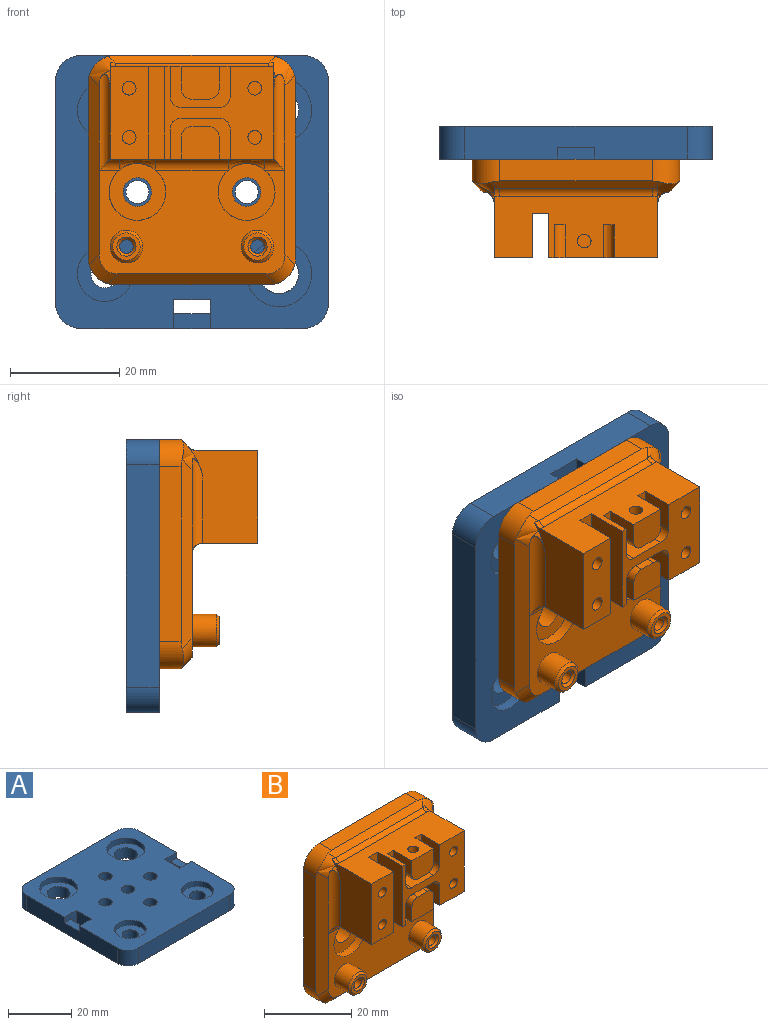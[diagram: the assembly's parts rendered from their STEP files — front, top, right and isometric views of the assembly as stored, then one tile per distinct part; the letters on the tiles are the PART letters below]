
ASSEMBLY  parts=2 mates=1
PART A: 37 faces, bbox 50x50x6 mm
  f0: cylinder r=2.55mm len=5.1mm, axis (0,0,-1), area 64.1mm2, adj f5,f26
  f1: cylinder r=2.55mm len=5.1mm, axis (0,0,-1), area 64.1mm2, adj f5,f24
  f2: cylinder r=3.6mm len=7.2mm, axis (0,0,-1), area 90.5mm2, adj f5,f22
  f3: cylinder r=3.6mm len=7.2mm, axis (0,0,-1), area 90.5mm2, adj f5,f20
  f4: plane 50x50mm, normal (0,0,1), area 1955.5mm2, adj f6,f7,f8,f9,f10,f11,f12,f13
  f5: plane 50x50mm, normal (0,0,-1), area 2256.5mm2, adj f0,f1,f2,f3,f6,f7,f8,f9
  f6: cylinder r=4.63mm len=6mm, axis (0,0,-1), area 43.7mm2, adj f4,f5,f7,f13
  f7: plane 40.73x6mm, normal (-1,0,0), area 229.8mm2, adj f4,f5,f6,f8,f27,f29,f30
  f8: cylinder r=4.63mm len=6mm, axis (0,0,-1), area 43.7mm2, adj f4,f5,f7,f9
  f9: plane 40.73x6mm, normal (0,-1,0), area 244.4mm2, adj f4,f5,f8,f10
  f10: cylinder r=4.63mm len=6mm, axis (0,0,-1), area 43.7mm2, adj f4,f5,f9,f11
  f11: plane 40.73x6mm, normal (1,0,0), area 229.8mm2, adj f4,f5,f10,f12,f31,f32,f34
  f12: cylinder r=4.63mm len=6mm, axis (0,0,-1), area 43.7mm2, adj f4,f5,f11,f13
  f13: plane 40.73x6mm, normal (0,1,0), area 244.4mm2, adj f4,f5,f6,f12
  f14: cylinder r=2.1mm len=6mm, axis (0,0,1), area 79.2mm2, adj f4,f5
  f15: cylinder r=2.1mm len=6mm, axis (0,0,1), area 79.2mm2, adj f4,f5
  f16: cylinder r=2.1mm len=6mm, axis (0,0,1), area 79.2mm2, adj f4,f5
  f17: cylinder r=2.1mm len=6mm, axis (0,0,1), area 79.2mm2, adj f4,f5
  f18: cylinder r=2.1mm len=6mm, axis (0,0,1), area 79.2mm2, adj f4,f5
  f19: cylinder r=6mm len=12mm, axis (0,0,1), area 75.4mm2, adj f4,f20
  f20: plane 12x12mm, normal (0,0,1), area 72.4mm2, adj f3,f19
  f21: cylinder r=6mm len=12mm, axis (0,0,1), area 75.4mm2, adj f4,f22
  f22: plane 12x12mm, normal (0,0,1), area 72.4mm2, adj f2,f21
  f23: cylinder r=5.05mm len=10.1mm, axis (0,0,1), area 63.5mm2, adj f4,f24
  f24: plane 10.1x10.1mm, normal (0,0,1), area 59.7mm2, adj f1,f23
  f25: cylinder r=5.05mm len=10.1mm, axis (0,0,1), area 63.5mm2, adj f4,f26
  f26: plane 10.1x10.1mm, normal (0,0,1), area 59.7mm2, adj f0,f25
  f27: plane 6x5.25mm, normal (0,-1,0), area 21mm2, adj f4,f5,f7,f28,f30,f35
  f28: plane 6.7x6mm, normal (-1,0,0), area 40.2mm2, adj f4,f5,f27,f29
  f29: plane 6x5.25mm, normal (0,1,0), area 21mm2, adj f4,f5,f7,f28,f30,f35
  f30: plane 6.7x2.75mm, normal (0,0,1), area 18.4mm2, adj f7,f27,f29,f35
  f31: plane 6x5.25mm, normal (0,-1,0), area 21mm2, adj f4,f5,f11,f33,f34,f36
  f32: plane 6x5.25mm, normal (0,1,0), area 21mm2, adj f4,f5,f11,f33,f34,f36
  f33: plane 6.7x6mm, normal (1,0,0), area 40.2mm2, adj f4,f5,f31,f32
  f34: plane 6.7x2.75mm, normal (0,0,1), area 18.4mm2, adj f11,f31,f32,f36
  f35: plane 6.7x3.82mm, normal (1,0,0), area 25.6mm2, adj f5,f27,f29,f30
  f36: plane 6.7x3.82mm, normal (-1,0,0), area 25.6mm2, adj f5,f31,f32,f34
PART B: 87 faces, bbox 39.9x19.9x43.9 mm
  f0: plane 35.89x20.89mm, normal (0,-1,0), area 425.8mm2, adj f10,f12,f14,f16,f53,f55,f56,f60
  f1: plane 32x4mm, normal (-1,0,0), area 128mm2, adj f9,f53,f57,f59
  f2: plane 28x4mm, normal (0,0,-1), area 112mm2, adj f9,f55,f59,f63
  f3: plane 32x4mm, normal (1,0,0), area 128mm2, adj f9,f56,f61,f63
  f4: cylinder r=2.6mm len=5.2mm, axis (0,-1,0), area 65.3mm2, adj f9,f13
  f5: cylinder r=1.25mm len=10.5mm, axis (0,-1,0), area 82.5mm2, adj f9,f65
  f6: cylinder r=1.25mm len=10.5mm, axis (0,-1,0), area 82.5mm2, adj f9,f67
  f7: plane 28x4mm, normal (0,0,1), area 112mm2, adj f9,f54,f57,f61
  f8: cylinder r=2.6mm len=5.2mm, axis (0,-1,0), area 65.3mm2, adj f9,f11
  f9: plane 42x38mm, normal (0,1,0), area 1522.2mm2, adj f1,f2,f3,f4,f5,f6,f7,f8
  f10: cylinder r=5.2mm len=10.4mm, axis (0,-1,0), area 65.3mm2, adj f0,f11,f82
  f11: plane 10.4x10.4mm, normal (0,-1,0), area 63.7mm2, adj f8,f10
  f12: cylinder r=5.2mm len=10.4mm, axis (0,-1,0), area 65.3mm2, adj f0,f13,f84
  f13: plane 10.4x10.4mm, normal (0,-1,0), area 63.7mm2, adj f4,f12
  f14: cylinder r=3mm len=6mm, axis (0,1,0), area 84.8mm2, adj f0,f68
  f15: plane 5x5mm, normal (0,-1,0), area 10mm2, adj f67,f68
  f16: cylinder r=3mm len=6mm, axis (0,1,0), area 84.8mm2, adj f0,f66
  f17: plane 5x5mm, normal (0,-1,0), area 10mm2, adj f65,f66
  f18: plane 18.53x13.59mm, normal (-1,0,0), area 174.4mm2, adj f19,f23,f24,f58,f77,f86
  f19: plane 30x10.4mm, normal (0,0,-1), area 249.7mm2, adj f18,f20,f24,f27,f28,f30,f31,f37
  f20: plane 17x8mm, normal (1,0,0), area 136mm2, adj f19,f23,f24,f50
  f21: cylinder r=1.25mm len=12mm, axis (0,1,0), area 94.2mm2, adj f24,f25
  f22: cylinder r=1.25mm len=12mm, axis (0,1,0), area 94.2mm2, adj f24,f26
  f23: plane 30x11.23mm, normal (0,0,1), area 282.3mm2, adj f18,f20,f24,f27,f31,f32,f34,f37
  f24: plane 17x7mm, normal (0,-1,0), area 109.2mm2, adj f18,f19,f20,f21,f22,f23
  f25: plane 2.5x2.5mm, normal (0,-1,0), area 4.9mm2, adj f21
  f26: plane 2.5x2.5mm, normal (0,-1,0), area 4.9mm2, adj f22
  f27: plane 17x8mm, normal (-1,0,0), area 136mm2, adj f19,f23,f37,f50
  f28: plane 6x5.5mm, normal (1,0,0), area 33mm2, adj f19,f37,f49,f74
  f29: plane 7x6mm, normal (0,0,-1), area 42mm2, adj f37,f49,f73,f74
  f30: plane 6x5.5mm, normal (-1,0,0), area 33mm2, adj f19,f37,f49,f73
  f31: plane 18.53x13.59mm, normal (1,0,0), area 174.4mm2, adj f19,f23,f37,f62,f79,f80
  f32: plane 6x5.5mm, normal (-1,0,0), area 33mm2, adj f23,f37,f48,f72
  f33: plane 7x6mm, normal (0,0,1), area 42mm2, adj f37,f48,f71,f72
  f34: plane 6x5.5mm, normal (1,0,0), area 33mm2, adj f23,f37,f48,f71
  f35: cylinder r=1.25mm len=12mm, axis (0,1,0), area 94.2mm2, adj f37,f39
  f36: cylinder r=1.25mm len=12mm, axis (0,1,0), area 94.2mm2, adj f37,f38
  f37: plane 20x17mm, normal (0,-1,0), area 168.6mm2, adj f19,f23,f27,f28,f29,f30,f31,f32
  f38: plane 2.5x2.5mm, normal (0,-1,0), area 4.9mm2, adj f36
  f39: plane 2.5x2.5mm, normal (0,-1,0), area 4.9mm2, adj f35
  f40: plane 6x4mm, normal (-1,0,0), area 24mm2, adj f23,f43,f48,f75
  f41: plane 6x3mm, normal (0,0,-1), area 13.1mm2, adj f43,f48,f51,f75,f76
  f42: plane 6x4mm, normal (1,0,0), area 24mm2, adj f23,f43,f48,f76
  f43: plane 7x6mm, normal (0,-1,0), area 40.3mm2, adj f23,f40,f41,f42,f75,f76
  f44: plane 6x4mm, normal (-1,0,0), area 24mm2, adj f19,f47,f49,f69
  f45: plane 6x4mm, normal (1,0,0), area 24mm2, adj f19,f47,f49,f70
  f46: plane 6x3mm, normal (0,0,1), area 13.1mm2, adj f47,f49,f52,f69,f70
  f47: plane 7x6mm, normal (0,-1,0), area 40.3mm2, adj f19,f44,f45,f46,f69,f70
  f48: plane 11x7.5mm, normal (0,-1,0), area 40.5mm2, adj f23,f32,f33,f34,f40,f41,f42,f71
  f49: plane 11x7.5mm, normal (0,-1,0), area 40.5mm2, adj f19,f28,f29,f30,f44,f45,f46,f69
  f50: plane 17x3mm, normal (0,-1,0), area 51mm2, adj f19,f20,f23,f27
  f51: cylinder r=1.25mm len=6mm, axis (0,0,1), area 47.1mm2, adj f23,f41
  f52: cylinder r=1.25mm len=6mm, axis (0,0,-1), area 47.1mm2, adj f19,f46
  f53: plane 34.67x2.08mm, normal (-0.71,-0.71,0), area 92.9mm2, adj f0,f1,f57,f58,f59,f60,f86
  f54: plane 30.67x1.5mm, normal (0,-0.71,0.71), area 58.8mm2, adj f7,f57,f58,f61,f62,f78
  f55: plane 30.67x2.08mm, normal (0,-0.71,-0.71), area 81.6mm2, adj f0,f2,f59,f60,f63,f64
  f56: plane 34.67x2.08mm, normal (0.71,-0.71,0), area 92.9mm2, adj f0,f3,f61,f62,f63,f64,f80
  f57: cylinder r=5mm len=5mm, axis (0,1,0), area 32.5mm2, adj f1,f7,f9,f53,f54,f58
  f58: cylinder r=5mm len=7.37mm, axis (-0.58,0.58,0.58), area 12.9mm2, adj f18,f53,f54,f57,f77,f86
  f59: cylinder r=5mm len=5mm, axis (0,-1,0), area 32.5mm2, adj f1,f2,f9,f53,f55,f60
  f60: cylinder r=5mm len=5.37mm, axis (-0.58,0.58,-0.58), area 16.6mm2, adj f0,f53,f55,f59
  f61: cylinder r=5mm len=5mm, axis (0,-1,0), area 32.5mm2, adj f3,f7,f9,f54,f56,f62
  f62: cylinder r=5mm len=7.37mm, axis (-0.58,-0.58,-0.58), area 12.9mm2, adj f31,f54,f56,f61,f79,f80
  f63: cylinder r=5mm len=5mm, axis (0,1,0), area 32.5mm2, adj f2,f3,f9,f55,f56,f64
  f64: cylinder r=5mm len=5.37mm, axis (-0.58,-0.58,0.58), area 16.6mm2, adj f0,f55,f56,f63
  f65: cone r=1.25mm half-angle=45deg, axis (0,-1,0), area 6.7mm2, adj f5,f17
  f66: cone r=2.5mm half-angle=45deg, axis (0,1,0), area 12.2mm2, adj f16,f17
  f67: cone r=1.25mm half-angle=45deg, axis (0,-1,0), area 6.7mm2, adj f6,f15
  f68: cone r=2.5mm half-angle=45deg, axis (0,1,0), area 12.2mm2, adj f14,f15
  f69: cylinder r=2mm len=6mm, axis (0,1,0), area 18.8mm2, adj f44,f46,f47,f49
  f70: cylinder r=2mm len=6mm, axis (0,1,0), area 18.8mm2, adj f45,f46,f47,f49
  f71: cylinder r=2mm len=6mm, axis (0,-1,0), area 18.8mm2, adj f33,f34,f37,f48
  f72: cylinder r=2mm len=6mm, axis (0,1,0), area 18.8mm2, adj f32,f33,f37,f48
  f73: cylinder r=2mm len=6mm, axis (0,-1,0), area 18.8mm2, adj f29,f30,f37,f49
  f74: cylinder r=2mm len=6mm, axis (0,-1,0), area 18.8mm2, adj f28,f29,f37,f49
  f75: cylinder r=2mm len=6mm, axis (0,1,0), area 18.8mm2, adj f40,f41,f43,f48
  f76: cylinder r=2mm len=6mm, axis (0,-1,0), area 18.8mm2, adj f41,f42,f43,f48
  f77: bspline ~1.59x1.16mm, area 1.6mm2, adj f18,f23,f58,f78
  f78: cylinder r=2mm len=28.1mm, axis (-1,0,0), area 44.1mm2, adj f23,f54,f77,f79
  f79: bspline ~1.59x1.16mm, area 1.6mm2, adj f23,f31,f62,f78
  f80: cylinder r=2mm len=17.55mm, axis (0,0,1), area 49.4mm2, adj f31,f56,f62,f81
  f81: cylinder r=2mm len=3.68mm, axis (1,0,0), area 8.4mm2, adj f0,f19,f80,f82
  f82: bspline ~6.65x2mm, area 15.3mm2, adj f10,f19,f81,f83
  f83: cylinder r=2mm len=13.35mm, axis (1,0,0), area 42mm2, adj f0,f19,f82,f84
  f84: bspline ~6.65x2mm, area 15.3mm2, adj f12,f19,f83,f85
  f85: cylinder r=2mm len=3.68mm, axis (1,0,0), area 8.4mm2, adj f0,f19,f84,f86
  f86: cylinder r=2mm len=17.55mm, axis (0,0,-1), area 49.4mm2, adj f18,f53,f58,f85
PLACE A rot(axis=(0.58,0.58,-0.58),120deg) t=(-4.75,0.84,0.67)mm
PLACE B rot(axis=(0.01,-1,-0.09),0deg) t=(-4.75,-11.16,0.67)mm
MATE fastened B.f4 <-> A.f15  axis (0,1,0) through (-14.75,-5.16,0.67)mm
